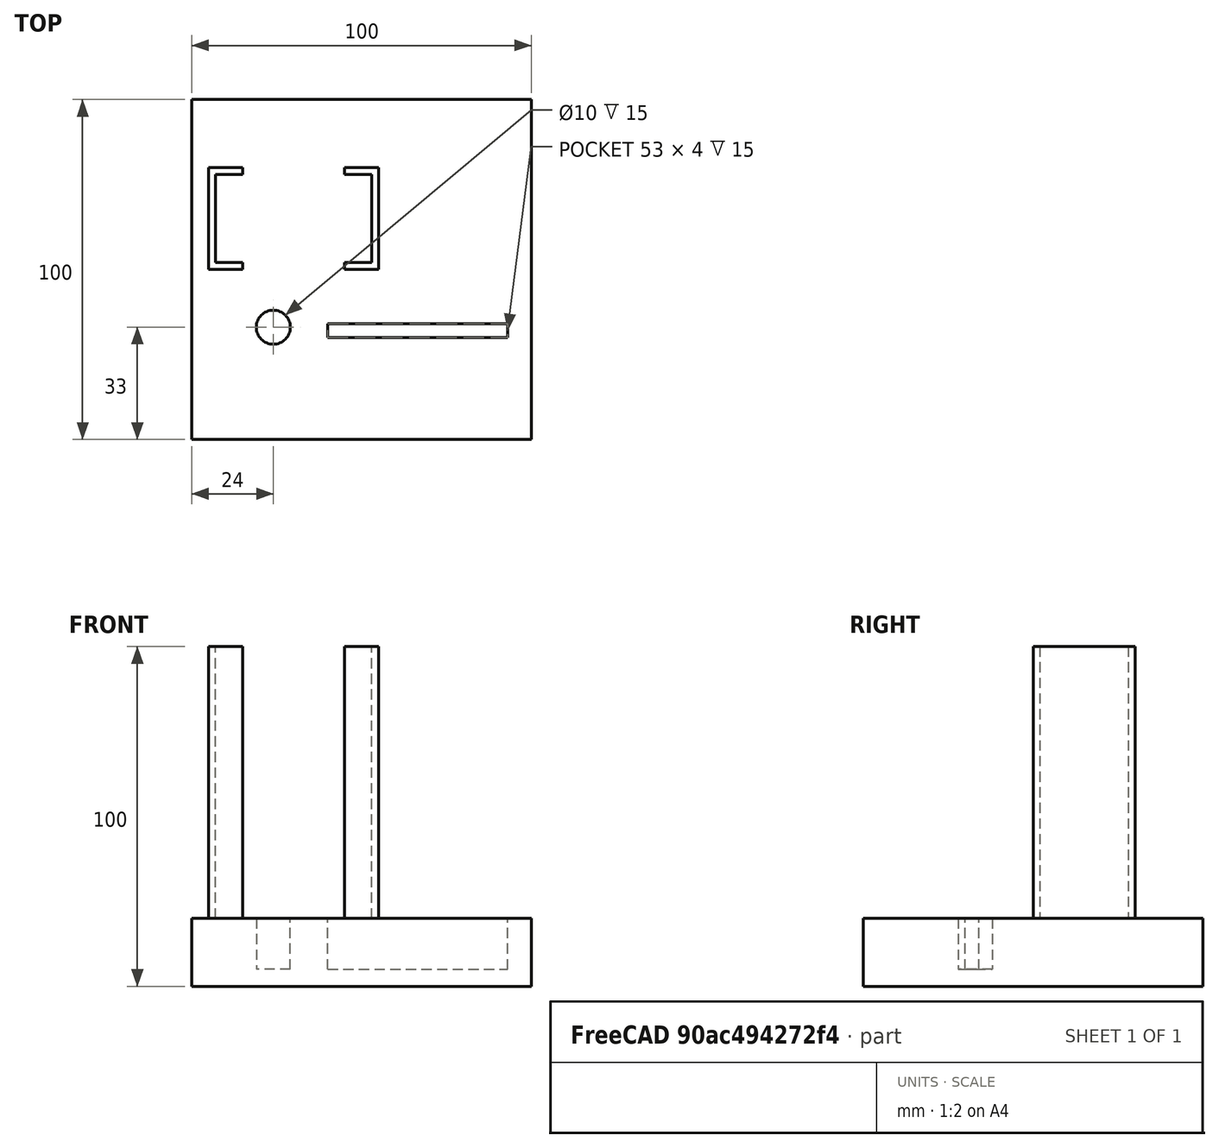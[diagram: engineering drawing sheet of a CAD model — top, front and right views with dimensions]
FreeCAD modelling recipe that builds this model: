
FCSTD DOCUMENT  (FreeCAD 0.20R29603 (Git))
Label: base
License: All rights reserved
LicenseURL: http://en.wikipedia.org/wiki/All_rights_reserved
objects: PartDesign::SubtractiveBox×3, PartDesign::AdditiveBox×2, PartDesign::SubtractiveCylinder×1, PartDesign::Body×1
note: 13 computed .brp shape members not serialized (recipe doc carries the construction recipe); baked Part::Feature solids carry a one-line shape summary decoded from their .brp

FEATURE [PartDesign::AdditiveBox] Box
  AttacherType = Attacher::AttachEngine3D
  Height = 20
  Length = 100
  MapMode = 5
  Support = -> [XY_Plane]
  Width = 100
FEATURE [PartDesign::SubtractiveCylinder] Cylinder
  Angle = 360
  AttacherType = Attacher::AttachEngine3D
  AttachmentOffset = pos=(24,33,-15) rot=(0,0,1;0rad)
  BaseFeature = -> Box
  FirstAngle = 0
  Height = 15
  MapMode = 5
  Placement = pos=(24,33,5) rot=(0,0,1;0rad)
  Radius = 5
  SecondAngle = 0
  Support = -> [Box]
FEATURE [PartDesign::AdditiveBox] Box001
  AttacherType = Attacher::AttachEngine3D
  AttachmentOffset = pos=(5,50,0) rot=(0,0,1;0rad)
  BaseFeature = -> Cylinder
  Height = 80
  Length = 50
  MapMode = 5
  Placement = pos=(5,50,20) rot=(0,0,1;0rad)
  Support = -> [Box]
  Width = 30
FEATURE [PartDesign::SubtractiveBox] Box002
  AttacherType = Attacher::AttachEngine3D
  AttachmentOffset = pos=(2,2,0) rot=(0,0,1;0rad)
  BaseFeature = -> Box001
  Height = 80
  Length = 46
  MapMode = 2
  Placement = pos=(7,52,20) rot=(0,0,1;0rad)
  Support = -> [Box001]
  Width = 26
FEATURE [PartDesign::SubtractiveBox] Box003
  AttacherType = Attacher::AttachEngine3D
  AttachmentOffset = pos=(8,-2,0) rot=(0,0,1;0rad)
  BaseFeature = -> Box002
  Height = 80
  Length = 30
  MapMode = 2
  Placement = pos=(15,50,20) rot=(0,0,1;0rad)
  Support = -> [Box002]
  Width = 30
FEATURE [PartDesign::SubtractiveBox] Box004
  AttacherType = Attacher::AttachEngine3D
  AttachmentOffset = pos=(40,30,5) rot=(0,0,1;0rad)
  BaseFeature = -> Box003
  Height = 15
  Length = 53
  MapMode = 2
  Placement = pos=(40,30,5) rot=(0,0,1;0rad)
  Support = -> [Box]
  Width = 4
FEATURE [PartDesign::Body] Body
  Group = -> [Box,Cylinder,Box001,Box002,Box003,Box004]
  Origin = -> Origin
  Tip = -> Box004
